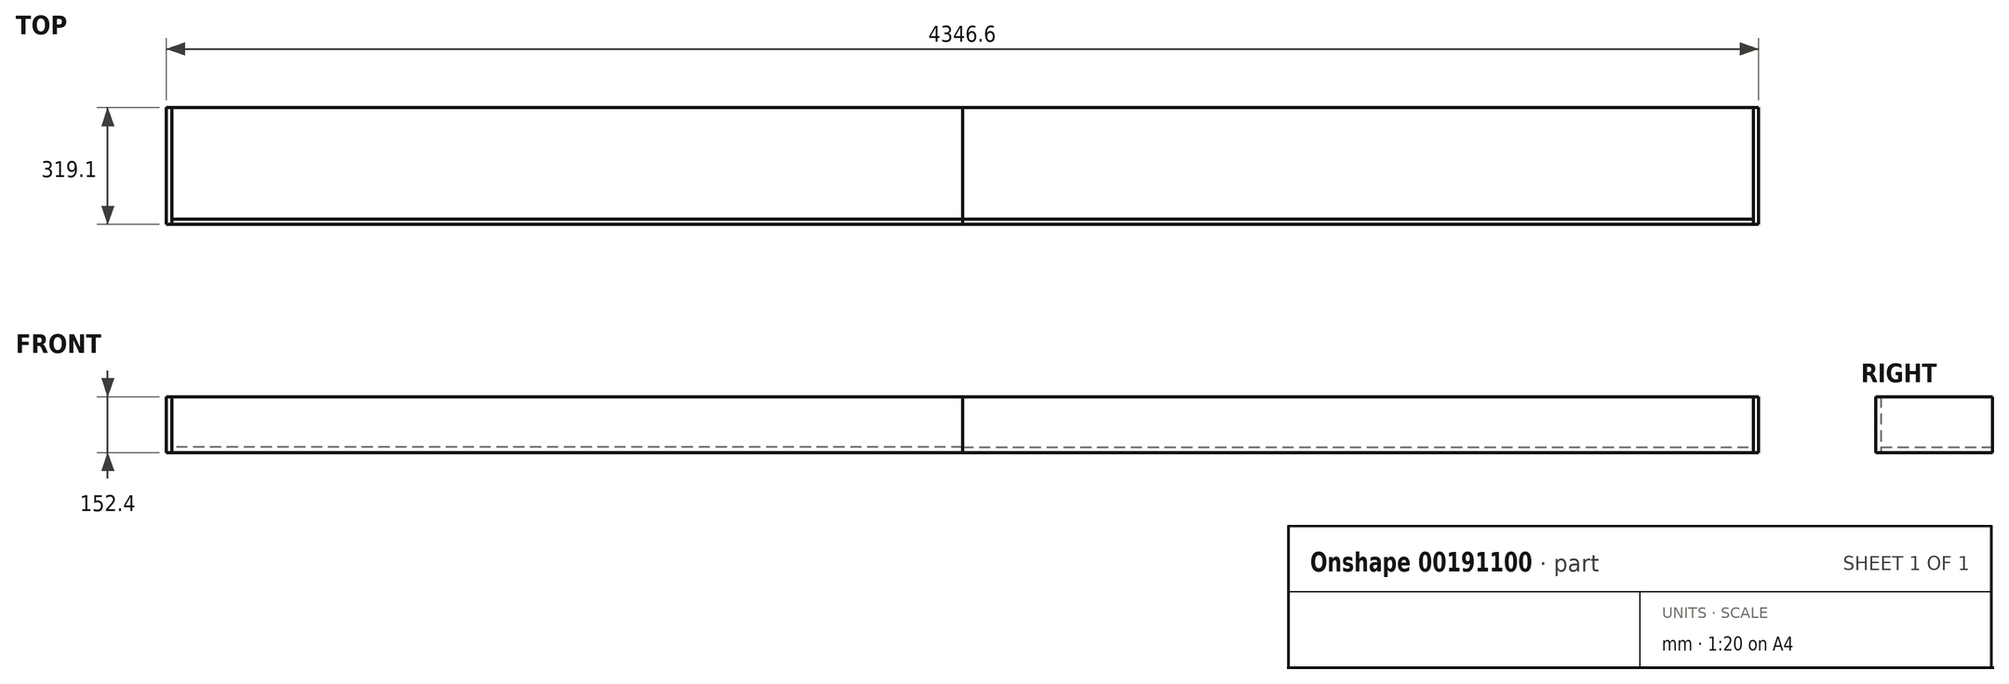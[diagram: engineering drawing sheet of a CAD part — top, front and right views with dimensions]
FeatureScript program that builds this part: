
annotation { "Feature Type Name" : "Feature", "Feature Type Description" : "" }
export const myFeature = defineFeature(function(context is Context, id is Id, definition is map)
    precondition{}
    {
        {
            var Q0;
            Q0=qCreatedBy(makeId("Top.planeOp"),FACE);
            var sketch = newSketch(context, id + "F0", { "sketchPlane" : qUnion([Q0])});
            skLineSegment(sketch, "E0.bottom", {"start": v(0, 0) * mm, "end": v(-2159, 0) * mm});
            skLineSegment(sketch, "E0.top", {"start": v(0, 304.8) * mm, "end": v(-2159, 304.8) * mm});
            skLineSegment(sketch, "E0.left", {"start": v(0, 0) * mm, "end": v(0, 304.8) * mm});
            skLineSegment(sketch, "E0.right", {"start": v(-2159, 0) * mm, "end": v(-2159, 304.8) * mm});
            skSolve(sketch);
        }
        {
            var Q0;
            Q0 = qSketchRegion(id + "F0", true);
            extrude(context, id + "F1", {"entities" : qUnion([Q0]), "depth" : 14.3 * mm});
        }
        {
            var Q0;
            Q0=qCreatedBy(makeId("Top.planeOp"),FACE);
            var sketch = newSketch(context, id + "F2", { "sketchPlane" : qUnion([Q0])});
            skLineSegment(sketch, "E1.bottom", {"start": v(0, 0) * mm, "end": v(2159, 0) * mm});
            skLineSegment(sketch, "E1.top", {"start": v(0, 304.8) * mm, "end": v(2159, 304.8) * mm});
            skLineSegment(sketch, "E1.left", {"start": v(0, 0) * mm, "end": v(0, 304.8) * mm});
            skLineSegment(sketch, "E1.right", {"start": v(2159, 0) * mm, "end": v(2159, 304.8) * mm});
            skSolve(sketch);
        }
        {
            var Q0;
            Q0 = qSketchRegion(id + "F2", true);
            extrude(context, id + "F3", {"entities" : qUnion([Q0]), "depth" : 14.3 * mm});
        }
        {
            var Q0;
            Q0=makeQuery(id+"F1.opExtrude","SWEPT_FACE",FACE,{"disambiguationData":[OSD([sQuery(id+"F0.wireOp",EDGE,"E0.bottom")])]});
            var sketch = newSketch(context, id + "F4", { "sketchPlane" : qUnion([Q0])});
            skLineSegment(sketch, "E2.bottom", {"start": v(-2159, 0) * mm, "end": v(0, 0) * mm});
            skLineSegment(sketch, "E2.top", {"start": v(-2159, 152.4) * mm, "end": v(0, 152.4) * mm});
            skLineSegment(sketch, "E2.left", {"start": v(-2159, 0) * mm, "end": v(-2159, 152.4) * mm});
            skLineSegment(sketch, "E2.right", {"start": v(0, 0) * mm, "end": v(0, 152.4) * mm});
            skSolve(sketch);
        }
        {
            var Q0;
            Q0 = qSketchRegion(id + "F4", true);
            extrude(context, id + "F5", {"entities" : qUnion([Q0]), "depth" : 13.6 * mm});
        }
        {
            var Q0;
            Q0=qCreatedBy(makeId("Front.planeOp"),FACE);
            var sketch = newSketch(context, id + "F6", { "sketchPlane" : qUnion([Q0])});
            skLineSegment(sketch, "E3.bottom", {"start": v(0, 0) * mm, "end": v(2159, 0) * mm});
            skLineSegment(sketch, "E3.top", {"start": v(0, 152.4) * mm, "end": v(2159, 152.4) * mm});
            skLineSegment(sketch, "E3.left", {"start": v(0, 0) * mm, "end": v(0, 152.4) * mm});
            skLineSegment(sketch, "E3.right", {"start": v(2159, 0) * mm, "end": v(2159, 152.4) * mm});
            skSolve(sketch);
        }
        {
            var Q0;
            Q0 = qSketchRegion(id + "F6", true);
            extrude(context, id + "F7", {"entities" : qUnion([Q0]), "depth" : 14.3 * mm});
        }
        {
            var Q0;
            Q0=makeQuery(id+"F1.opExtrude","SWEPT_FACE",FACE,{"disambiguationData":[OSD([sQuery(id+"F0.wireOp",EDGE,"E0.right")])]});
            var sketch = newSketch(context, id + "F8", { "sketchPlane" : qUnion([Q0])});
            skLineSegment(sketch, "E4", {"start": v(14.3, 0) * mm, "end": v(14.3, 172.1) * mm, "construction": true});
            skLineSegment(sketch, "E5.bottom", {"start": v(14.3, 0) * mm, "end": v(-304.8, 0) * mm});
            skLineSegment(sketch, "E5.top", {"start": v(14.3, 152.4) * mm, "end": v(-304.8, 152.4) * mm});
            skLineSegment(sketch, "E5.left", {"start": v(14.3, 0) * mm, "end": v(14.3, 152.4) * mm});
            skLineSegment(sketch, "E5.right", {"start": v(-304.8, 0) * mm, "end": v(-304.8, 152.4) * mm});
            skSolve(sketch);
        }
        {
            var Q0;
            Q0 = qSketchRegion(id + "F8", true);
            extrude(context, id + "F9", {"entities" : qUnion([Q0]), "depth" : 14.3 * mm});
        }
        {
            var Q0;
            Q0=makeQuery(id+"F3.opExtrude","SWEPT_FACE",FACE,{"disambiguationData":[OSD([sQuery(id+"F2.wireOp",EDGE,"E1.right")])]});
            var sketch = newSketch(context, id + "F10", { "sketchPlane" : qUnion([Q0])});
            skLineSegment(sketch, "E6", {"start": v(-14.3, 0) * mm, "end": v(-14.3, 186.6) * mm, "construction": true});
            skLineSegment(sketch, "E7.bottom", {"start": v(-14.3, 0) * mm, "end": v(304.8, 0) * mm});
            skLineSegment(sketch, "E7.top", {"start": v(-14.3, 152.4) * mm, "end": v(304.8, 152.4) * mm});
            skLineSegment(sketch, "E7.left", {"start": v(-14.3, 0) * mm, "end": v(-14.3, 152.4) * mm});
            skLineSegment(sketch, "E7.right", {"start": v(304.8, 0) * mm, "end": v(304.8, 152.4) * mm});
            skSolve(sketch);
        }
        {
            var Q0;
            Q0 = qSketchRegion(id + "F10", true);
            extrude(context, id + "F11", {"entities" : qUnion([Q0]), "depth" : 14.3 * mm});
        }
    });
